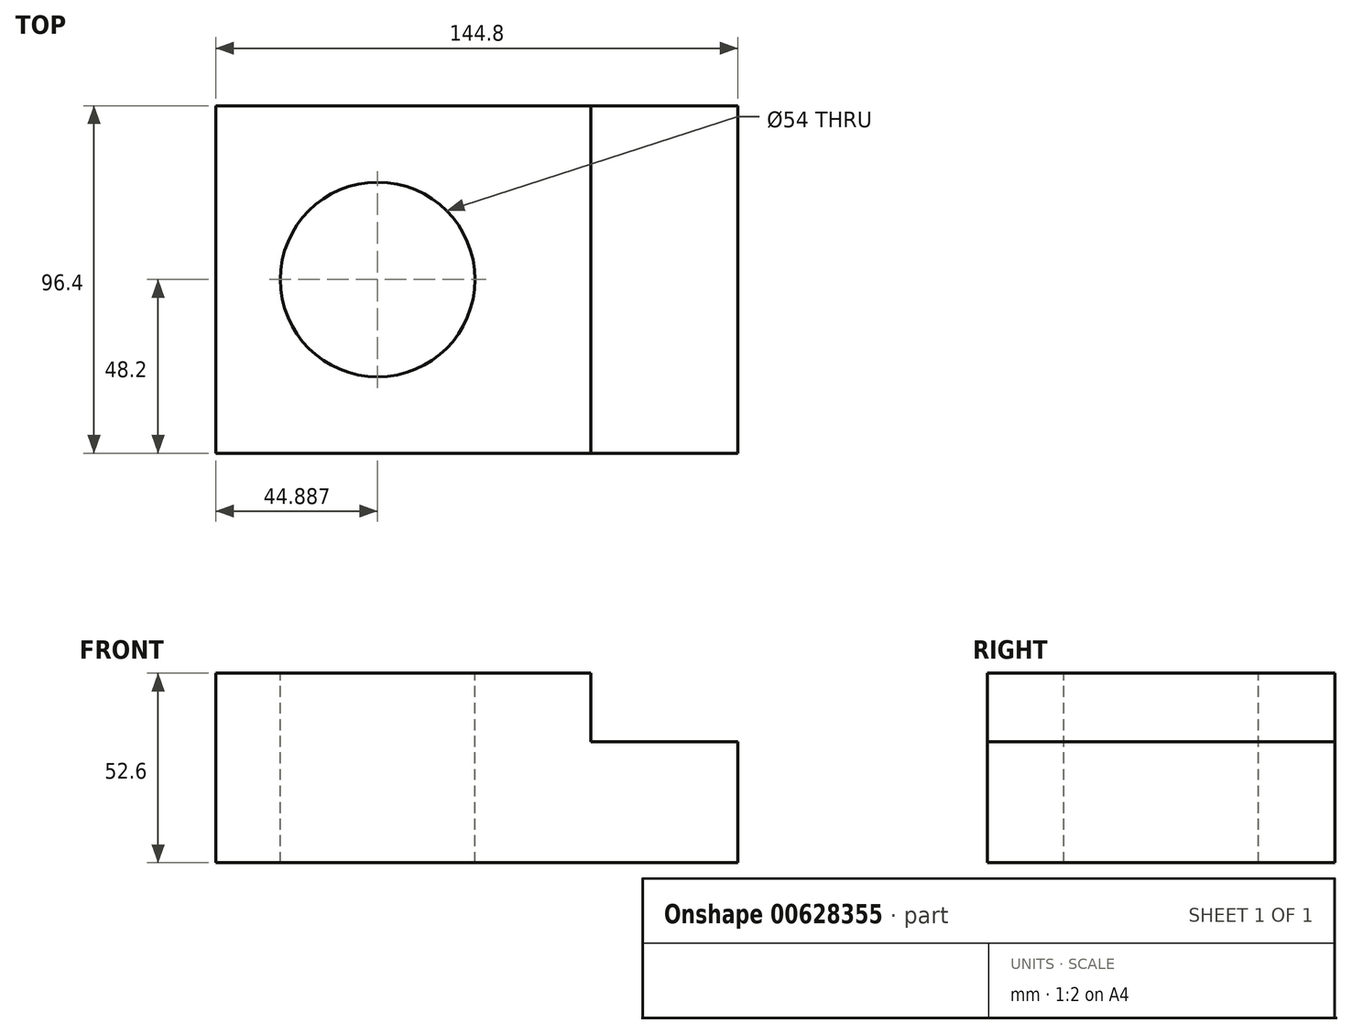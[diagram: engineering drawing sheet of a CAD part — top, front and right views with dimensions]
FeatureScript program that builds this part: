
annotation { "Feature Type Name" : "Feature", "Feature Type Description" : "" }
export const myFeature = defineFeature(function(context is Context, id is Id, definition is map)
    precondition{}
    {
        {
            var Q0;
            Q0=qCreatedBy(makeId("Top.planeOp"),FACE);
            var sketch = newSketch(context, id + "F0", { "sketchPlane" : qUnion([Q0])});
            skLineSegment(sketch, "E0.bottom", {"start": v(-72.4, 48.2) * mm, "end": v(72.4, 48.2) * mm});
            skLineSegment(sketch, "E0.top", {"start": v(-72.4, -48.2) * mm, "end": v(72.4, -48.2) * mm});
            skLineSegment(sketch, "E0.left", {"start": v(-72.4, 48.2) * mm, "end": v(-72.4, -48.2) * mm});
            skLineSegment(sketch, "E0.right", {"start": v(72.4, 48.2) * mm, "end": v(72.4, -48.2) * mm});
            skPoint(sketch, "E0.middle", {"position": v(0, 0) * mm});
            skSolve(sketch);
        }
        {
            var Q0;
            Q0=makeQuery(id+"F0.imprint","IMPRINT",FACE,{"disambiguationData":[TD([[makeQuery(id+"F0.imprint","IMPRINT",EDGE,{"derivedFrom":sQuery(id+"F0.wireOp",EDGE,"E0.bottom")}),-1.0]])]});
            extrude(context, id + "F1", {"entities" : qUnion([Q0]), "depth" : 33.6 * mm, "offsetDistance" : 25 * mm});
        }
        {
            var Q0;
            Q0=makeQuery(id+"F1.opExtrude","CAP_FACE",FACE,{"disambiguationData":[OSD([sQuery(id+"F0.wireOp",EDGE,"E0.bottom"),sQuery(id+"F0.wireOp",EDGE,"E0.top"),sQuery(id+"F0.wireOp",EDGE,"E0.left"),sQuery(id+"F0.wireOp",EDGE,"E0.right")])],"isStart":false});
            var sketch = newSketch(context, id + "F2", { "sketchPlane" : qUnion([Q0])});
            skLineSegment(sketch, "E1.bottom", {"start": v(-72.4, 48.2) * mm, "end": v(31.6, 48.2) * mm});
            skLineSegment(sketch, "E1.top", {"start": v(-72.4, -48.2) * mm, "end": v(31.6, -48.2) * mm});
            skLineSegment(sketch, "E1.left", {"start": v(-72.4, 48.2) * mm, "end": v(-72.4, -48.2) * mm});
            skLineSegment(sketch, "E1.right", {"start": v(31.6, 48.2) * mm, "end": v(31.6, -48.2) * mm});
            skPoint(sketch, "E1.middle", {"position": v(-20.4, 0) * mm});
            skSolve(sketch);
        }
        {
            var Q0;
            Q0 = qSketchRegion(id + "F2", true);
            extrude(context, id + "F3", {"entities" : qUnion([Q0]), "operationType" : NewBodyOperationType.ADD, "depth" : 19 * mm, "offsetDistance" : 25 * mm});
        }
        {
            var Q0;
            Q0=makeQuery(id+"F3.opExtrude","CAP_FACE",FACE,{"disambiguationData":[OSD([sQuery(id+"F2.wireOp",EDGE,"E1.bottom"),sQuery(id+"F2.wireOp",EDGE,"E1.top"),sQuery(id+"F2.wireOp",EDGE,"E1.left"),sQuery(id+"F2.wireOp",EDGE,"E1.right")])],"isStart":false});
            var sketch = newSketch(context, id + "F4", { "sketchPlane" : qUnion([Q0])});
            skCircle(sketch, "E2", {"center": v(-27.51, 0) * mm, "radius": 27 * mm});
            skSolve(sketch);
        }
        {
            var Q0;
            Q0=makeQuery(id+"F4.imprint","IMPRINT",FACE,{"disambiguationData":[TD([[makeQuery(id+"F4.imprint","IMPRINT",EDGE,{"derivedFrom":sQuery(id+"F4.wireOp",EDGE,"E2")}),1.0]])]});
            extrude(context, id + "F5", {"entities" : qUnion([Q0]), "operationType" : NewBodyOperationType.REMOVE, "oppositeDirection" : true, "depth" : 159 * mm, "offsetDistance" : 25 * mm});
        }
    });
